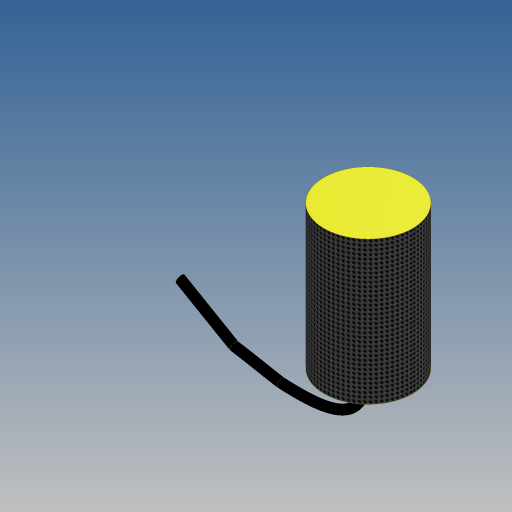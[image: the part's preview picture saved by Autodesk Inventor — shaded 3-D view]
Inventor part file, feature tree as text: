
AUTODESK INVENTOR PART (.ipt)
format: ipt  version: 2023.3 (Build 273359000, 359)  size: 231,936 bytes
history: native  units: mm
features: sketch x4, extrude x1, hole x1, sweep x1, revolve x1
ambient origin geometry x8: Origin, YZ Plane, XZ Plane, XY Plane, X Axis, Y Axis, Z Axis, Center Point
bodies: Volumenkörper1 (feature_tree)
feature tree (8):
  extrude  "Extrusion1"  Depth=102.0mm TaperAngle=0.0deg
  hole  "Bohrung1"  [1 undecoded]
  sweep  "Sweeping1"
  revolve  "Umdrehung1"
  sketch  "Skizze1"  dims[d0=63.0mm d1=102.0mm d2=0.0mm]
  sketch  "Skizze2"  dims[d3=18.5mm]
  sketch  "Skizze6"  dims[d4=8.376mm d5=20.0mm d6=4.0mm d7=2.0mm d8=90.0deg d9=27.3mm d10=20.594885mm d20=6.0mm]
  sketch  "Skizze10"  dims[d21=0.0mm d22=0.0mm d27=60.0deg d29=300.0mm d33=600.0mm d34=4.20773mm d35=65.0mm d36=60.5875mm d37=90.0deg]
note: 1 required parameter value undecoded (feature->parameter linkage not recoverable at this tier; creation-order binding heuristic only, values carry confidence <= 0.55)
